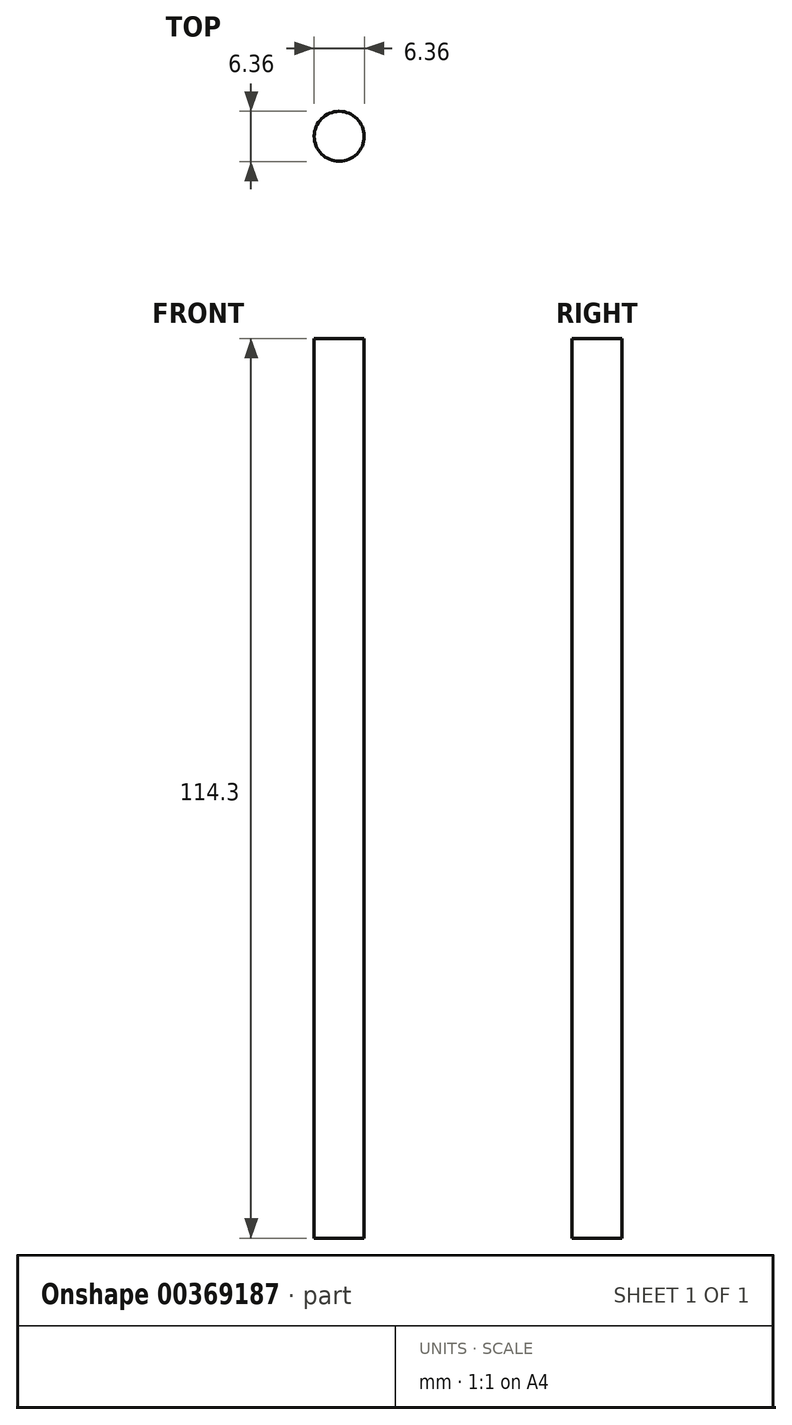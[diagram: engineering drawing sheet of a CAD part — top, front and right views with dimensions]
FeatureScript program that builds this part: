
annotation { "Feature Type Name" : "Feature", "Feature Type Description" : "" }
export const myFeature = defineFeature(function(context is Context, id is Id, definition is map)
    precondition{}
    {
        {
            var Q0;
            Q0=qCreatedBy(makeId("Top.planeOp"),FACE);
            var sketch = newSketch(context, id + "F0", { "sketchPlane" : qUnion([Q0])});
            skCircle(sketch, "E0", {"center": v(0, 0) * mm, "radius": 3.18 * mm});
            skSolve(sketch);
        }
        {
            var Q0;
            Q0 = qSketchRegion(id + "F0", true);
            extrude(context, id + "F1", {"entities" : qUnion([Q0]), "depth" : 114.3 * mm});
        }
    });
